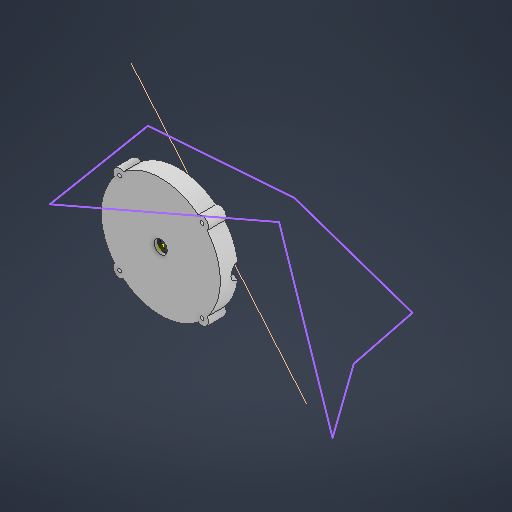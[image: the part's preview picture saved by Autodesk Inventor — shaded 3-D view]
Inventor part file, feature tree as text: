
AUTODESK INVENTOR PART (.ipt)
format: ipt  version: 2025.3 (Build 293356030, 356C)  size: 269,824 bytes
history: native  units: mm
features: sketch x6, extrude x4, plane x2, other x1
ambient origin geometry x8: Origin, YZ Plane, XZ Plane, XY Plane, X Axis, Y Axis, Z Axis, Center Point
bodies: Solid1 (feature_tree)
feature tree (13):
  sketch  "Sketch1"  dims[d1=40.0mm]
  extrude  "Extrusion1"  Depth=10.0mm TaperAngle=0.0deg
  extrude  "Extrusion2"  Depth=13.75mm TaperAngle=0.0deg
  extrude  "Extrusion3"  Depth=10.0mm
  sketch  "Sketch2"  dims[d12=7.5mm d13=0.0mm d14=13.75mm d15=0.0mm]
  plane  "Work Plane1"
  sketch  "Sketch3"  dims[d16=-13.089969mm d21=10.0mm]
  plane  "Work Plane3"
  extrude  "Extrusion5"  Depth=10.65mm
  other  "Work Axis1"
  sketch  "Sketch6"  dims[d24=20.0mm d25=0.0mm]
  sketch  "Sketch Circular Pattern1"  dims[d2=10.0mm d3=16.9mm d4=85.0mm d5=90.0mm d6=2.9mm d7=5.0mm d8=360.0deg d9=92.0mm d10=2.5mm d11=0.0mm]
  sketch  "Sketch5"  dims[d22=30.0deg d23=10.65mm]
